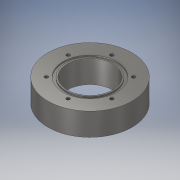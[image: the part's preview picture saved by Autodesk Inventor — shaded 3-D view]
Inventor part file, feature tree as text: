
AUTODESK INVENTOR PART (.ipt)
format: ipt  version: 2018 (Build 220112000, 112)  size: 190,464 bytes
history: native  units: in
note: dims shown in document units (in); Inventor stores cm internally (conversion verified against a paired STEP export)
features: sketch x5, extrude x4, hole x1, chamfer x1, pattern_circular x1
ambient origin geometry x8: Origin, YZ Plane, XZ Plane, XY Plane, X Axis, Y Axis, Z Axis, Center Point
bodies: Solid1 (feature_tree)
feature tree (12):
  extrude  "Extrusion1"  Depth=0.5in TaperAngle=0.0deg
  extrude  "Extrusion2"  Depth=0.03in
  extrude  "Extrusion3"  Depth=0.03in
  extrude  "Extrusion4"  Depth=0.03in
  hole  "Hole1"  [1 undecoded]
  chamfer  "Chamfer1"  Distance=0.68in
  pattern_circular  "Circular Pattern1"  Angle=45.0deg  [1 undecoded]
  sketch  "Sketch1"  dims[d0=1.85in d1=0.5in d2=0.0in]
  sketch  "Sketch2"  dims[d3=0.03in d4=0.06in]
  sketch  "Sketch3"  dims[d5=0.03in d6=0.0in d7=1.0in]
  sketch  "Sketch4"  dims[d8=0.05in d9=0.0in d10=0.03in]
  sketch  "Sketch5"  dims[d11=0.06in d12=0.03in d13=0.0in d14=0.68in d15=45.0deg d16=0.13in d17=0.328in d18=0.375in d19=0.25in d20=0.5635in d21=0.484in d22=0.8108in d23=2.3622in d24=360.0deg d26=0.015in d27=0.125in d28=45.0deg]
note: 2 required parameter values undecoded (feature->parameter linkage not recoverable at this tier; creation-order binding heuristic only, values carry confidence <= 0.55)
